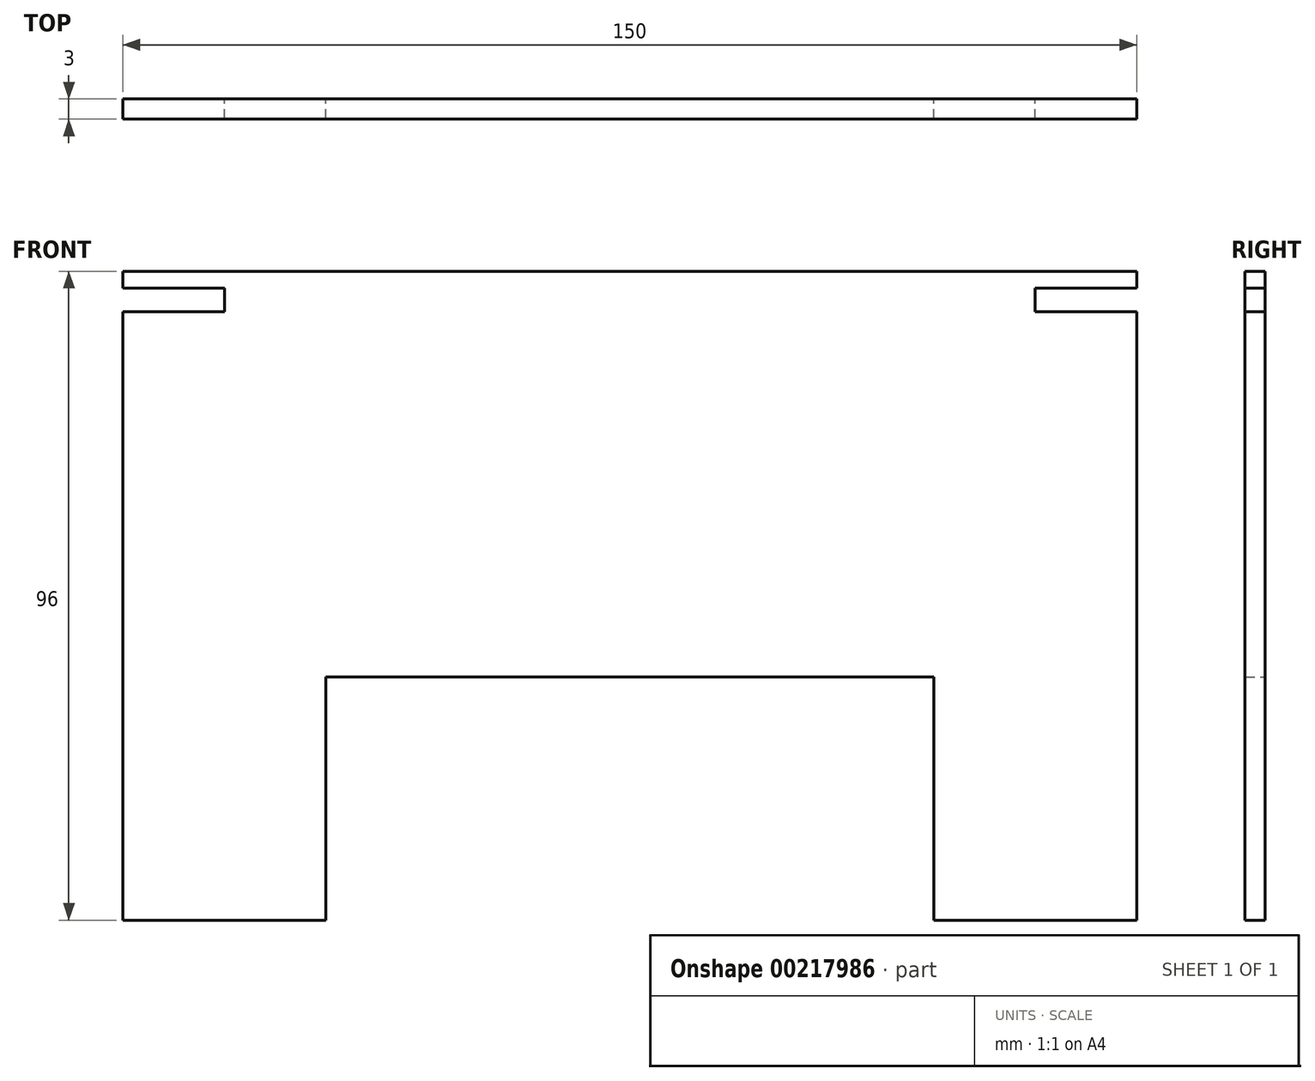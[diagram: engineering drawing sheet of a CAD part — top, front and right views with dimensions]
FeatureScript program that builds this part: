
annotation { "Feature Type Name" : "Feature", "Feature Type Description" : "" }
export const myFeature = defineFeature(function(context is Context, id is Id, definition is map)
    precondition{}
    {
        {
            var Q0;
            Q0=qCreatedBy(makeId("Front.planeOp"),FACE);
            var sketch = newSketch(context, id + "F0", { "sketchPlane" : qUnion([Q0])});
            skLineSegment(sketch, "E0", {"start": v(84.07, -36) * mm, "end": v(54.07, -36) * mm});
            skLineSegment(sketch, "E1", {"start": v(54.07, -36) * mm, "end": v(54.07, 0) * mm});
            skLineSegment(sketch, "E2", {"start": v(54.07, 0) * mm, "end": v(-35.93, 0) * mm});
            skLineSegment(sketch, "E3", {"start": v(-35.93, 0) * mm, "end": v(-35.93, -36) * mm});
            skLineSegment(sketch, "E4", {"start": v(-35.93, -36) * mm, "end": v(-65.93, -36) * mm});
            skLineSegment(sketch, "E5.bottom", {"start": v(84.07, 57.5) * mm, "end": v(69.07, 57.5) * mm});
            skLineSegment(sketch, "E5.top", {"start": v(84.07, 54) * mm, "end": v(69.07, 54) * mm});
            skLineSegment(sketch, "E5.right", {"start": v(69.07, 57.5) * mm, "end": v(69.07, 54) * mm});
            skLineSegment(sketch, "E6.bottom", {"start": v(-50.93, 57.5) * mm, "end": v(-50.93, 57.5) * mm});
            skLineSegment(sketch, "E6.top", {"start": v(-65.93, 54) * mm, "end": v(-50.93, 54) * mm});
            skLineSegment(sketch, "E6.right", {"start": v(-50.93, 57.5) * mm, "end": v(-50.93, 54) * mm});
            skLineSegment(sketch, "E7", {"start": v(-50.93, 62.5) * mm, "end": v(-50.93, 57.5) * mm});
            skLineSegment(sketch, "E8", {"start": v(-65.93, 54) * mm, "end": v(-65.93, -36) * mm});
            skLineSegment(sketch, "E9", {"start": v(84.07, 57.5) * mm, "end": v(84.07, 60) * mm});
            skLineSegment(sketch, "E10", {"start": v(84.07, 54) * mm, "end": v(84.07, -36) * mm});
            skLineSegment(sketch, "E11", {"start": v(-50.93, 57.5) * mm, "end": v(-65.93, 57.5) * mm});
            skLineSegment(sketch, "E12", {"start": v(-65.93, 57.5) * mm, "end": v(-65.93, 60) * mm});
            skLineSegment(sketch, "E13", {"start": v(-65.93, 60) * mm, "end": v(84.07, 60) * mm});
            skSolve(sketch);
        }
        {
            var Q0;
            Q0 = qSketchRegion(id + "F0", true);
            extrude(context, id + "F1", {"entities" : qUnion([Q0]), "depth" : 3 * mm});
        }
    });
